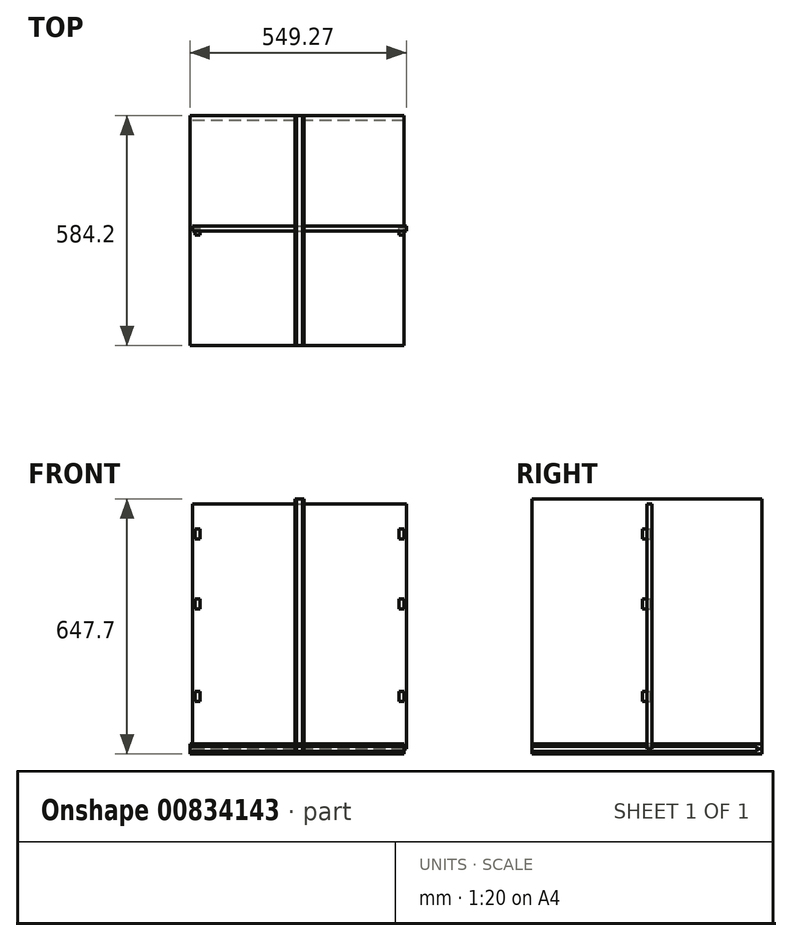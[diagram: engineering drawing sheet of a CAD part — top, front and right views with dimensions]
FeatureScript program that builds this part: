
annotation { "Feature Type Name" : "Feature", "Feature Type Description" : "" }
export const myFeature = defineFeature(function(context is Context, id is Id, definition is map)
    precondition{}
    {
        {
            assignVariable(context, id + "F0", {"name" : "Width", "anyValue" : 22.38});
        }
        {
            assignVariable(context, id + "F1", {"name" : "Height", "anyValue" : 25.5});
        }
        {
            assignVariable(context, id + "F2", {"name" : "Length", "anyValue" : 23});
        }
        {
            var Q0;
            Q0=qCreatedBy(makeId("Top.planeOp"),FACE);
            var sketch = newSketch(context, id + "F3", { "sketchPlane" : qUnion([Q0])});
            skLineSegment(sketch, "E0.bottom", {"start": v(277.81, 292.1) * mm, "end": v(-277.81, 292.1) * mm});
            skLineSegment(sketch, "E0.top", {"start": v(277.81, -292.1) * mm, "end": v(-277.81, -292.1) * mm});
            skLineSegment(sketch, "E0.left", {"start": v(277.81, 292.1) * mm, "end": v(277.81, -292.1) * mm});
            skLineSegment(sketch, "E0.right", {"start": v(-277.81, 292.1) * mm, "end": v(-277.81, -292.1) * mm});
            skPoint(sketch, "E0.middle", {"position": v(0, 0) * mm});
            skSolve(sketch);
        }
        {
            var Q0;
            Q0=makeQuery(id+"F3.imprint","IMPRINT",FACE,{"disambiguationData":[TD([[makeQuery(id+"F3.imprint","IMPRINT",EDGE,{"derivedFrom":sQuery(id+"F3.wireOp",EDGE,"E0.bottom")}),1.0]])]});
            extrude(context, id + "F4", {"entities" : qUnion([Q0]), "depth" : 19.05 * mm});
        }
        {
            var Q0;
            Q0=makeQuery(id+"F4.opExtrude","SWEPT_FACE",FACE,{"disambiguationData":[OSD([sQuery(id+"F3.wireOp",EDGE,"E0.right")])]});
            var sketch = newSketch(context, id + "F5", { "sketchPlane" : qUnion([Q0])});
            skLineSegment(sketch, "E1.bottom", {"start": v(-292.1, 19.05) * mm, "end": v(-279.4, 19.05) * mm});
            skLineSegment(sketch, "E1.top", {"start": v(-292.1, 12.7) * mm, "end": v(-279.4, 12.7) * mm});
            skLineSegment(sketch, "E1.left", {"start": v(-292.1, 19.05) * mm, "end": v(-292.1, 12.7) * mm});
            skLineSegment(sketch, "E1.right", {"start": v(-279.4, 19.05) * mm, "end": v(-279.4, 12.7) * mm});
            skSolve(sketch);
        }
        {
            var Q0;
            Q0=qSketchRegion(id+"F5",true);
            extrude(context, id + "F6", {"entities" : qUnion([Q0]), "operationType" : NewBodyOperationType.REMOVE, "endBound" : BoundingType.THROUGH_ALL, "oppositeDirection" : true, "depth" : 25.4 * mm});
        }
        {
            var Q0;
            Q0=qCreatedBy(makeId("Right.planeOp"),FACE);
            cPlane(context, id + "F7", {"entities" : qUnion([Q0]), "cplaneType" : CPlaneType.OFFSET, "offset" : (getVariable(context, 'Width') / 2) * mm, "width" : 152.4 * mm, "height" : 152.4 * mm});
        }
        {
            var Q0;
            Q0=qCreatedBy(id+"F7.planeOp",FACE);
            var sketch = newSketch(context, id + "F8", { "sketchPlane" : qUnion([Q0])});
            skLineSegment(sketch, "E2.bottom", {"start": v(-292.1, 0) * mm, "end": v(292.1, 0) * mm});
            skLineSegment(sketch, "E2.top", {"start": v(-292.1, 647.7) * mm, "end": v(292.1, 647.7) * mm});
            skLineSegment(sketch, "E2.left", {"start": v(-292.1, 0) * mm, "end": v(-292.1, 647.7) * mm});
            skLineSegment(sketch, "E2.right", {"start": v(292.1, 0) * mm, "end": v(292.1, 647.7) * mm});
            skPoint(sketch, "E2.middle", {"position": v(0, 323.85) * mm});
            skSolve(sketch);
        }
        {
            var Q0;
            Q0=qSketchRegion(id+"F8",true);
            extrude(context, id + "F9", {"entities" : qUnion([Q0]), "oppositeDirection" : true, "depth" : 19.05 * mm});
        }
        {
            var Q0;
            Q0=makeQuery(id+"F9.opExtrude","SWEPT_FACE",FACE,{"disambiguationData":[OSD([sQuery(id+"F8.wireOp",EDGE,"E2.top")])]});
            var sketch = newSketch(context, id + "F10", { "sketchPlane" : qUnion([Q0])});
            skLineSegment(sketch, "E3.bottom", {"start": v(265.11, 292.1) * mm, "end": v(271.46, 292.1) * mm});
            skLineSegment(sketch, "E3.top", {"start": v(265.11, 279.4) * mm, "end": v(271.46, 279.4) * mm});
            skLineSegment(sketch, "E3.left", {"start": v(265.11, 292.1) * mm, "end": v(265.11, 279.4) * mm});
            skLineSegment(sketch, "E3.right", {"start": v(271.46, 292.1) * mm, "end": v(271.46, 279.4) * mm});
            skSolve(sketch);
        }
        {
            var Q0;
            Q0=makeQuery(id+"F10.imprint","IMPRINT",FACE,{"disambiguationData":[TD([[makeQuery(id+"F10.imprint","IMPRINT",EDGE,{"derivedFrom":sQuery(id+"F10.wireOp",EDGE,"E3.bottom")}),-1.0]])]});
            extrude(context, id + "F11", {"entities" : qUnion([Q0]), "operationType" : NewBodyOperationType.REMOVE, "endBound" : BoundingType.THROUGH_ALL, "oppositeDirection" : true, "depth" : 25.4 * mm});
        }
        {
            var Q0;
            Q0=makeQuery(id+"F9.opExtrude","SWEPT_FACE",FACE,{"disambiguationData":[OSD([sQuery(id+"F8.wireOp",EDGE,"E2.left")])]});
            var sketch = newSketch(context, id + "F12", { "sketchPlane" : qUnion([Q0])});
            skLineSegment(sketch, "E4.bottom", {"start": v(265.11, 0) * mm, "end": v(277.81, 0) * mm});
            skLineSegment(sketch, "E4.top", {"start": v(265.11, 19.05) * mm, "end": v(277.81, 19.05) * mm});
            skLineSegment(sketch, "E4.left", {"start": v(265.11, 0) * mm, "end": v(265.11, 19.05) * mm});
            skLineSegment(sketch, "E4.right", {"start": v(277.81, 0) * mm, "end": v(277.81, 19.05) * mm});
            skLineSegment(sketch, "E5.bottom", {"start": v(265.11, 647.7) * mm, "end": v(277.81, 647.7) * mm});
            skLineSegment(sketch, "E5.top", {"start": v(265.11, 628.65) * mm, "end": v(277.81, 628.65) * mm});
            skLineSegment(sketch, "E5.left", {"start": v(265.11, 647.7) * mm, "end": v(265.11, 628.65) * mm});
            skLineSegment(sketch, "E5.right", {"start": v(277.81, 647.7) * mm, "end": v(277.81, 628.65) * mm});
            skSolve(sketch);
        }
        {
            var Q0;
            Q0=qSketchRegion(id+"F12",true);
            extrude(context, id + "F13", {"entities" : qUnion([Q0]), "operationType" : NewBodyOperationType.REMOVE, "endBound" : BoundingType.THROUGH_ALL, "oppositeDirection" : true, "depth" : 25.4 * mm});
        }
        {
            var Q0;
            Q0=qCreatedBy(makeId("Front.planeOp"),FACE);
            cPlane(context, id + "F14", {"entities" : qUnion([Q0]), "cplaneType" : CPlaneType.OFFSET, "offset" : (getVariable(context, 'Length') / 2) * mm, "oppositeDirection" : true, "width" : 152.4 * mm, "height" : 152.4 * mm});
        }
        {
            var Q0;
            Q0=qCreatedBy(id+"F14.planeOp",FACE);
            var sketch = newSketch(context, id + "F15", { "sketchPlane" : qUnion([Q0])});
            skLineSegment(sketch, "E6.bottom", {"start": v(-271.46, 12.7) * mm, "end": v(271.46, 12.7) * mm});
            skLineSegment(sketch, "E6.top", {"start": v(-271.46, 635) * mm, "end": v(271.46, 635) * mm});
            skLineSegment(sketch, "E6.left", {"start": v(-271.46, 12.7) * mm, "end": v(-271.46, 635) * mm});
            skLineSegment(sketch, "E6.right", {"start": v(271.46, 12.7) * mm, "end": v(271.46, 635) * mm});
            skPoint(sketch, "E6.middle", {"position": v(0, 323.85) * mm});
            skSolve(sketch);
        }
        {
            var Q0;
            Q0=makeQuery(id+"F15.imprint","IMPRINT",FACE,{"disambiguationData":[TD([[makeQuery(id+"F15.imprint","IMPRINT",EDGE,{"derivedFrom":sQuery(id+"F15.wireOp",EDGE,"E6.bottom")}),1.0]])]});
            extrude(context, id + "F16", {"entities" : qUnion([Q0]), "depth" : 12.7 * mm});
        }
        {
            var Q0;
            Q0=qCreatedBy(makeId("Top.planeOp"),FACE);
            cPlane(context, id + "F17", {"entities" : qUnion([Q0]), "cplaneType" : CPlaneType.OFFSET, "offset" : (getVariable(context, 'Height') / 2) * mm, "width" : 152.4 * mm, "height" : 152.4 * mm});
        }
        {
            var Q0;
            Q0=makeQuery(id+"F4.opExtrude","SWEPT_BODY",BODY,{"disambiguationData":[OSD([sQuery(id+"F3.wireOp",EDGE,"E0.bottom"),sQuery(id+"F3.wireOp",EDGE,"E0.top"),sQuery(id+"F3.wireOp",EDGE,"E0.left"),sQuery(id+"F3.wireOp",EDGE,"E0.right")])]});
            var Q1;
            Q1=qCreatedBy(id+"F17.planeOp",FACE);
            mirror(context, id + "F18", {"entities" : qUnion([Q0]), "mirrorPlane" : qUnion([Q1])});
        }
        {
            var Q0;
            Q0=makeQuery(id+"F9.opExtrude","SWEPT_BODY",BODY,{"disambiguationData":[OSD([sQuery(id+"F8.wireOp",EDGE,"E2.bottom"),sQuery(id+"F8.wireOp",EDGE,"E2.top"),sQuery(id+"F8.wireOp",EDGE,"E2.left"),sQuery(id+"F8.wireOp",EDGE,"E2.right")])]});
            var Q1;
            Q1=qCreatedBy(makeId("Right.planeOp"),FACE);
            mirror(context, id + "F19", {"entities" : qUnion([Q0]), "mirrorPlane" : qUnion([Q1])});
        }
        {
            var Q0;
            Q0=qCreatedBy(makeId("Front.planeOp"),FACE);
            var sketch = newSketch(context, id + "F20", { "sketchPlane" : qUnion([Q0])});
            skLineSegment(sketch, "E7.bottom", {"start": v(265.11, 158.75) * mm, "end": v(252.41, 158.75) * mm});
            skLineSegment(sketch, "E7.top", {"start": v(265.11, 133.35) * mm, "end": v(252.41, 133.35) * mm});
            skLineSegment(sketch, "E7.left", {"start": v(265.11, 158.75) * mm, "end": v(265.11, 133.35) * mm});
            skLineSegment(sketch, "E7.right", {"start": v(252.41, 158.75) * mm, "end": v(252.41, 133.35) * mm});
            skLineSegment(sketch, "E8.bottom", {"start": v(265.11, 393.7) * mm, "end": v(252.41, 393.7) * mm});
            skLineSegment(sketch, "E8.top", {"start": v(265.11, 368.3) * mm, "end": v(252.41, 368.3) * mm});
            skLineSegment(sketch, "E8.left", {"start": v(265.11, 393.7) * mm, "end": v(265.11, 368.3) * mm});
            skLineSegment(sketch, "E8.right", {"start": v(252.41, 393.7) * mm, "end": v(252.41, 368.3) * mm});
            skLineSegment(sketch, "E9.bottom", {"start": v(265.11, 571.5) * mm, "end": v(252.41, 571.5) * mm});
            skLineSegment(sketch, "E9.top", {"start": v(265.11, 546.1) * mm, "end": v(252.41, 546.1) * mm});
            skLineSegment(sketch, "E9.left", {"start": v(265.11, 571.5) * mm, "end": v(265.11, 546.1) * mm});
            skLineSegment(sketch, "E9.right", {"start": v(252.41, 571.5) * mm, "end": v(252.41, 546.1) * mm});
            skPoint(sketch, "E10", {"position": v(265.11, 146.05) * mm});
            skPoint(sketch, "E11", {"position": v(265.11, 381) * mm});
            skPoint(sketch, "E12", {"position": v(265.11, 558.8) * mm});
            skSolve(sketch);
        }
        {
            var Q0;
            Q0=qSketchRegion(id+"F20",true);
            extrude(context, id + "F21", {"entities" : qUnion([Q0]), "depth" : (getVariable(context, 'Length') / 2) * mm, "hasSecondDirection" : true, "secondDirectionOppositeDirection" : true, "secondDirectionDepth" : (18 - getVariable(context, 'Length') / 2) * mm});
        }
        {
            var Q0;
            Q0=makeQuery(id+"F21.opExtrude","SWEPT_BODY",BODY,{"disambiguationData":[OSD([sQuery(id+"F20.wireOp",EDGE,"E7.bottom"),sQuery(id+"F20.wireOp",EDGE,"E7.top"),sQuery(id+"F20.wireOp",EDGE,"E7.left"),sQuery(id+"F20.wireOp",EDGE,"E7.right")])]});
            var Q1;
            Q1=makeQuery(id+"F21.opExtrude","SWEPT_BODY",BODY,{"disambiguationData":[OSD([sQuery(id+"F20.wireOp",EDGE,"E8.bottom"),sQuery(id+"F20.wireOp",EDGE,"E8.top"),sQuery(id+"F20.wireOp",EDGE,"E8.left"),sQuery(id+"F20.wireOp",EDGE,"E8.right")])]});
            var Q2;
            Q2=makeQuery(id+"F21.opExtrude","SWEPT_BODY",BODY,{"disambiguationData":[OSD([sQuery(id+"F20.wireOp",EDGE,"E9.bottom"),sQuery(id+"F20.wireOp",EDGE,"E9.top"),sQuery(id+"F20.wireOp",EDGE,"E9.left"),sQuery(id+"F20.wireOp",EDGE,"E9.right")])]});
            var Q3;
            Q3=qCreatedBy(makeId("Right.planeOp"),FACE);
            mirror(context, id + "F22", {"entities" : qUnion([Q0, Q1, Q2]), "mirrorPlane" : qUnion([Q3])});
        }
    });
